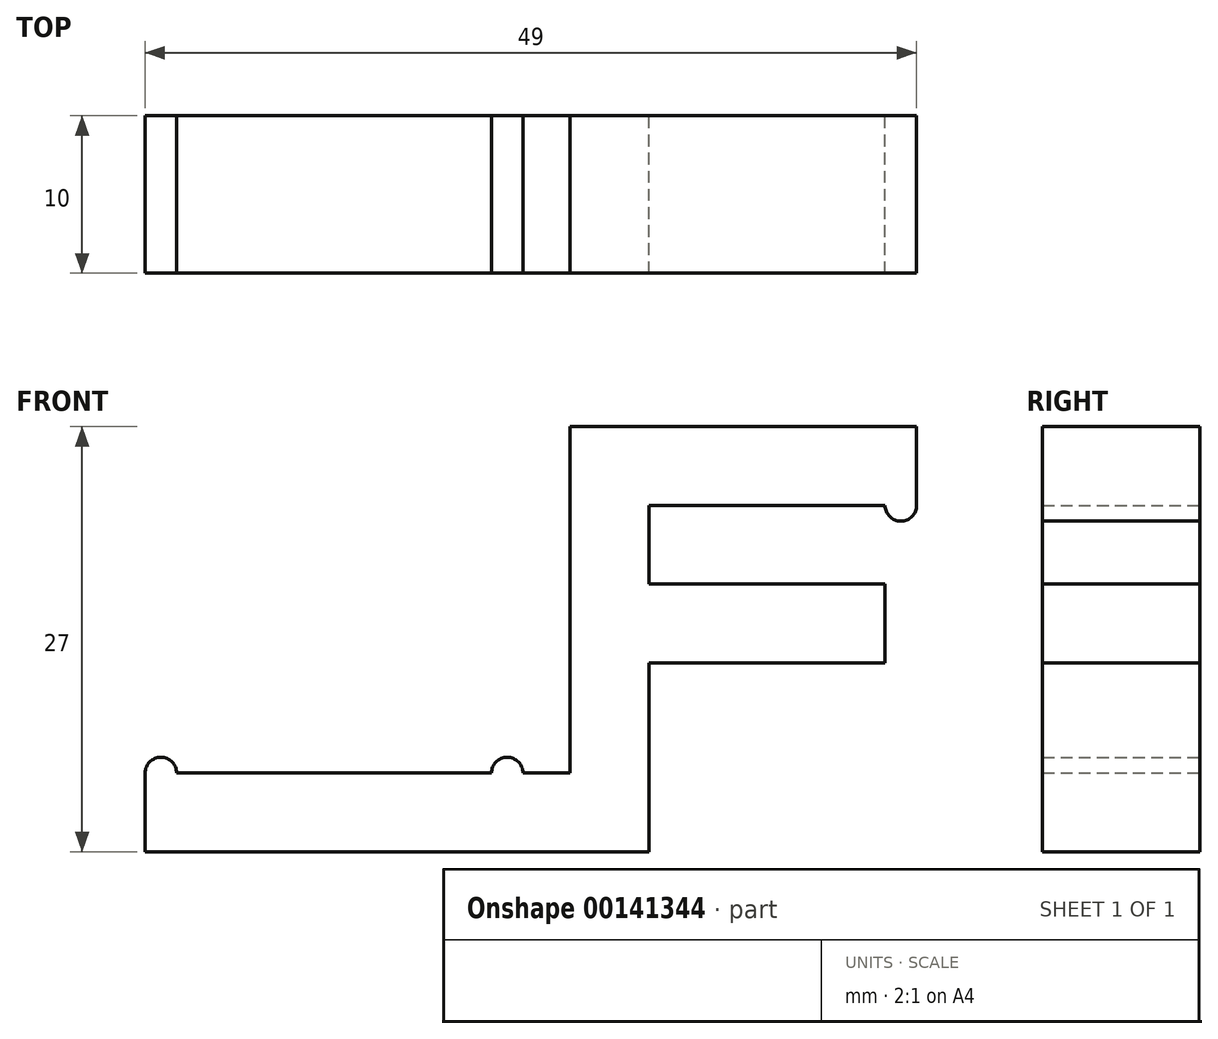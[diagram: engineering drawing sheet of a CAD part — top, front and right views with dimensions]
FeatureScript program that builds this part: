
annotation { "Feature Type Name" : "Feature", "Feature Type Description" : "" }
export const myFeature = defineFeature(function(context is Context, id is Id, definition is map)
    precondition{}
    {
        {
            var Q0;
            Q0=qCreatedBy(makeId("Front.planeOp"),FACE);
            var sketch = newSketch(context, id + "F0", { "sketchPlane" : qUnion([Q0])});
            skLineSegment(sketch, "E0.bottom", {"start": v(0, 0) * mm, "end": v(-32, 0) * mm});
            skLineSegment(sketch, "E0.top", {"start": v(0, 5) * mm, "end": v(-32, 5) * mm});
            skLineSegment(sketch, "E0.left", {"start": v(0, 0) * mm, "end": v(0, 5) * mm});
            skLineSegment(sketch, "E0.right", {"start": v(-32, 0) * mm, "end": v(-32, 5) * mm});
            skLineSegment(sketch, "E1.bottom", {"start": v(0, 5) * mm, "end": v(-5, 5) * mm});
            skLineSegment(sketch, "E1.top", {"start": v(0, 27) * mm, "end": v(-5, 27) * mm});
            skLineSegment(sketch, "E1.left", {"start": v(0, 5) * mm, "end": v(0, 27) * mm});
            skLineSegment(sketch, "E1.right", {"start": v(-5, 5) * mm, "end": v(-5, 27) * mm});
            skLineSegment(sketch, "E2.left", {"start": v(0, 27) * mm, "end": v(0, 27) * mm});
            skLineSegment(sketch, "E3.bottom", {"start": v(0, 27) * mm, "end": v(17, 27) * mm});
            skLineSegment(sketch, "E3.top", {"start": v(0, 22) * mm, "end": v(17, 22) * mm});
            skLineSegment(sketch, "E3.left", {"start": v(0, 27) * mm, "end": v(0, 22) * mm});
            skLineSegment(sketch, "E3.right", {"start": v(17, 27) * mm, "end": v(17, 22) * mm});
            skLineSegment(sketch, "E4.bottom", {"start": v(0, 17) * mm, "end": v(15, 17) * mm});
            skLineSegment(sketch, "E4.top", {"start": v(0, 12) * mm, "end": v(15, 12) * mm});
            skLineSegment(sketch, "E4.left", {"start": v(0, 17) * mm, "end": v(0, 12) * mm});
            skLineSegment(sketch, "E4.right", {"start": v(15, 17) * mm, "end": v(15, 12) * mm});
            skArc(sketch, "E5", {"start": v(-30, 5) * mm, "mid": v(-31, 6) * mm, "end": v(-32, 5) * mm});
            skArc(sketch, "E6", {"start": v(15, 22) * mm, "mid": v(16, 21) * mm, "end": v(17, 22) * mm});
            skArc(sketch, "E7", {"start": v(-8, 5) * mm, "mid": v(-9, 6) * mm, "end": v(-10, 5) * mm});
            skSolve(sketch);
        }
        {
            var Q0;
            Q0 = qSketchRegion(id + "F0", true);
            extrude(context, id + "F1", {"entities" : qUnion([Q0]), "depth" : 10 * mm});
        }
    });
